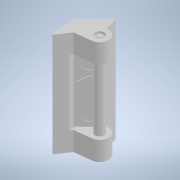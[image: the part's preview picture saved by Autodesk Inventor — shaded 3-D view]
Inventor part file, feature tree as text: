
AUTODESK INVENTOR PART (.ipt)
format: ipt  version: 2021 (Build 250183000, 183)  size: 192,000 bytes
history: native  units: mm
features: other x21, sketch x6, extrude x3, hole x2, revolve x1
ambient origin geometry x8: Origin, YZ Plane, XZ Plane, XY Plane, X Axis, Y Axis, Z Axis, Center Point
bodies: Solid1 (feature_tree)
feature tree (33):
  extrude  "Extrusion1"  Depth=22.1mm TaperAngle=0.0deg
  extrude  "Extrusion2"  TaperAngle=360.0deg  [1 undecoded]
  extrude  "Extrusion3"  TaperAngle=0.0deg  [1 undecoded]
  revolve  "Revolution1"  [1 undecoded]
  hole  "Hole1"  [1 undecoded]
  hole  "Hole2"  [1 undecoded]
  other  "to_bolt_XY"
  other  "to_bolt_YZ"
  other  "to_bolt_ZX"
  other  "to_bolt_X"
  other  "to_bolt_Y"
  other  "to_bolt_Z"
  other  "to_bolt_Center"
  other  "to_door_XY"
  other  "to_door_YZ"
  other  "to_door_ZX"
  other  "to_door_X"
  other  "to_door_Y"
  other  "to_door_Z"
  other  "to_door_Center"
  other  "to_frame_XY"
  other  "to_frame_YZ"
  other  "to_frame_ZX"
  other  "to_frame_X"
  other  "to_frame_Y"
  other  "to_frame_Z"
  other  "to_frame_Center"
  sketch  "Sketch_1"  dims[d0=35.0mm d1=0.0mm d2=22.1mm d3=0.0mm]
  sketch  "Sketch_2"  dims[d4=0.6mm d5=0.0mm d6=360.0deg]
  sketch  "Sketch_3"  dims[d7=4.21mm d8=6.0mm d9=4.0mm d10=2.0mm d11=90.0deg d12=0.2mm d13=0.0mm]
  sketch  "Sketch_4"  dims[d14=4.21mm d15=6.0mm d16=4.0mm d17=2.0mm d18=90.0deg d19=0.2mm d20=0.0mm d21=0.0mm]
  sketch  "Sketch5"
  sketch  "Sketch6"
note: 5 required parameter values undecoded (feature->parameter linkage not recoverable at this tier; creation-order binding heuristic only, values carry confidence <= 0.55)
